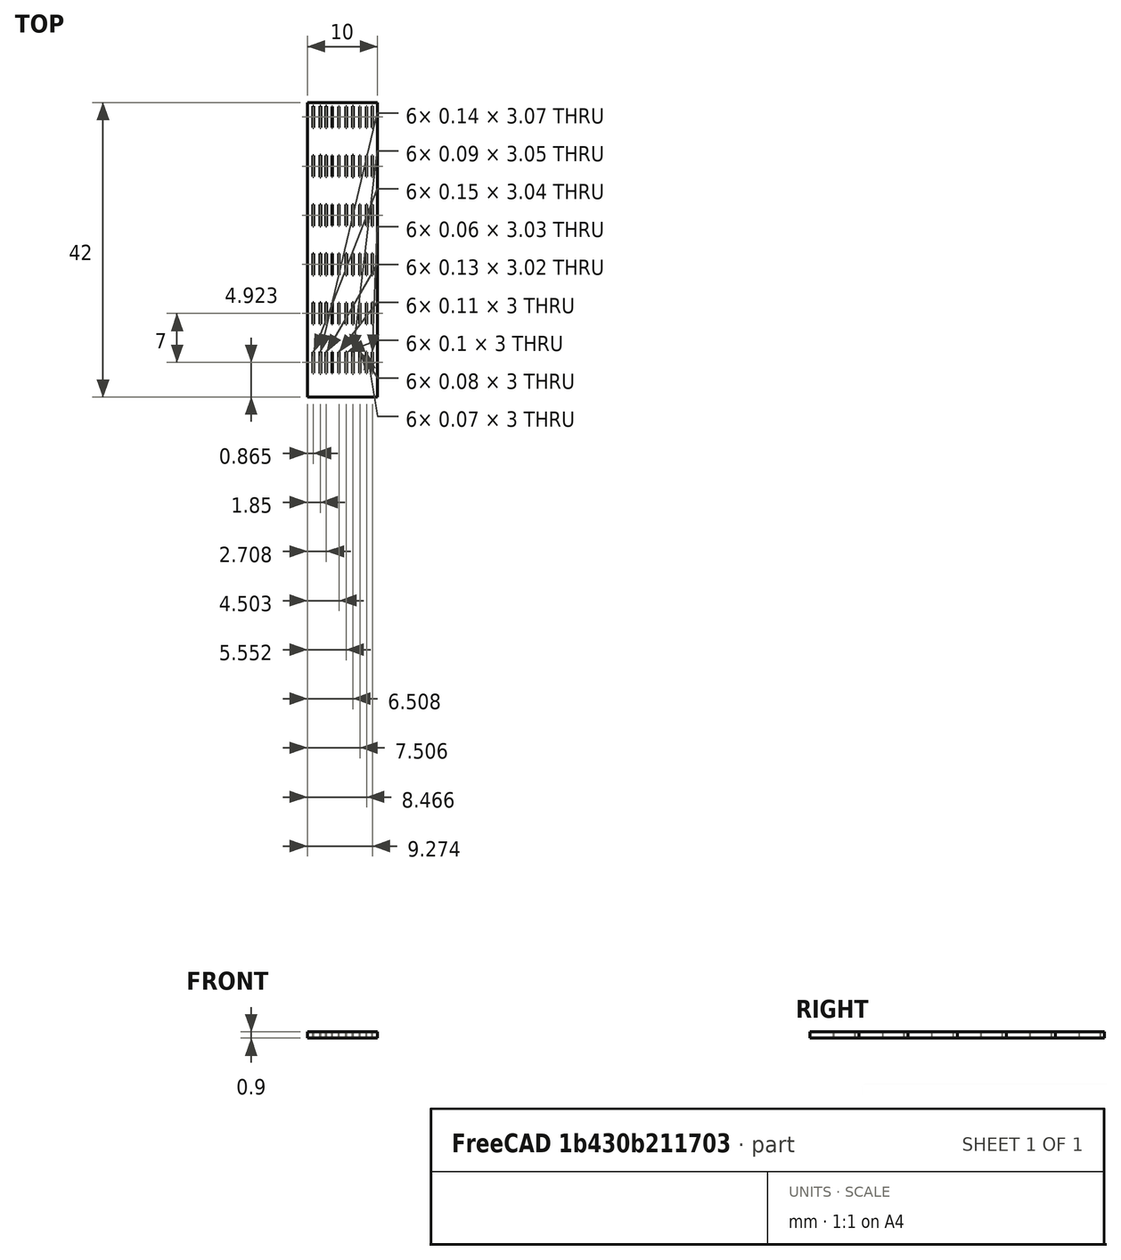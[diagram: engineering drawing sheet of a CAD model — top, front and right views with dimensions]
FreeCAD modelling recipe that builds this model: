
FCSTD DOCUMENT  (FreeCAD 0.20R29177 (Git))
Label: Slit test
License: All rights reserved
LicenseURL: http://en.wikipedia.org/wiki/All_rights_reserved
objects: Sketcher::SketchObject×1, PartDesign::Pad×1, PartDesign::LinearPattern×1, PartDesign::Body×1
note: 5 computed .brp shape members not serialized (recipe doc carries the construction recipe); baked Part::Feature solids carry a one-line shape summary decoded from their .brp

FEATURE [Sketcher::SketchObject] Sketch
  FullyConstrained = false
  MapMode = 5
  Support = -> [XY_Plane]
  sketch-geometry (44):
    g0: LineSegment StartX=0 StartY=0 StartZ=0 EndX=10.0001 EndY=0 EndZ=0
    g1: LineSegment StartX=10.0001 StartY=0 StartZ=0 EndX=10 EndY=7 EndZ=0
    g2: LineSegment StartX=10 StartY=7 StartZ=0 EndX=0 EndY=7 EndZ=0
    g3: LineSegment StartX=0 StartY=7 StartZ=0 EndX=0 EndY=0 EndZ=0
    g4: LineSegment StartX=8.4312 StartY=3.42473 StartZ=0 EndX=8.5012 EndY=3.42473 EndZ=0
    g5: LineSegment StartX=8.5012 StartY=3.42473 StartZ=0 EndX=8.5012 EndY=6.42151 EndZ=0
    g6: LineSegment StartX=8.5012 StartY=6.42151 StartZ=0 EndX=8.4312 EndY=6.42151 EndZ=0
    g7: LineSegment StartX=8.4312 StartY=6.42151 StartZ=0 EndX=8.4312 EndY=3.42473 EndZ=0
    g8: LineSegment StartX=7.54626 StartY=3.42473 StartZ=0 EndX=7.46626 EndY=3.42473 EndZ=0
    g9: LineSegment StartX=7.46626 StartY=3.42473 StartZ=0 EndX=7.46626 EndY=6.42151 EndZ=0
    g10: LineSegment StartX=7.46626 StartY=6.42151 StartZ=0 EndX=7.54626 EndY=6.42151 EndZ=0
    g11: LineSegment StartX=7.54626 StartY=6.42151 StartZ=0 EndX=7.54626 EndY=3.42473 EndZ=0
    g12: LineSegment StartX=5.60229 StartY=3.42473 StartZ=0 EndX=5.50229 EndY=3.42473 EndZ=0
    g13: LineSegment StartX=5.50229 StartY=3.42473 StartZ=0 EndX=5.50229 EndY=6.42151 EndZ=0
    g14: LineSegment StartX=5.50229 StartY=6.42151 StartZ=0 EndX=5.60229 EndY=6.42151 EndZ=0
    g15: LineSegment StartX=5.60229 StartY=6.42151 StartZ=0 EndX=5.60229 EndY=3.42473 EndZ=0
    g16: LineSegment StartX=4.55752 StartY=3.42473 StartZ=0 EndX=4.44752 EndY=3.42473 EndZ=0
    g17: LineSegment StartX=4.44752 StartY=3.42473 StartZ=0 EndX=4.44752 EndY=6.42151 EndZ=0
    g18: LineSegment StartX=4.44752 StartY=6.42151 StartZ=0 EndX=4.55752 EndY=6.42151 EndZ=0
    g19: LineSegment StartX=4.55752 StartY=6.42151 StartZ=0 EndX=4.55752 EndY=3.42473 EndZ=0
    g20: LineSegment StartX=3.60416 StartY=3.42473 StartZ=0 EndX=3.48416 EndY=3.42473 EndZ=0
    g21: LineSegment StartX=3.48416 StartY=3.42473 StartZ=0 EndX=3.48416 EndY=6.42151 EndZ=0
    g22: LineSegment StartX=3.48416 StartY=6.42151 StartZ=0 EndX=3.60416 EndY=6.42151 EndZ=0
    g23: LineSegment StartX=3.60416 StartY=6.42151 StartZ=0 EndX=3.60416 EndY=3.42473 EndZ=0
    g24: LineSegment StartX=9.24385 StartY=6.43941 StartZ=0 EndX=9.30385 EndY=6.43941 EndZ=0
    g25: LineSegment StartX=9.30385 StartY=6.43941 StartZ=0 EndX=9.30385 EndY=3.40683 EndZ=0
    g26: LineSegment StartX=9.30385 StartY=3.40683 StartZ=0 EndX=9.24385 EndY=3.40683 EndZ=0
    g27: LineSegment StartX=9.24385 StartY=3.40683 StartZ=0 EndX=9.24385 EndY=6.43941 EndZ=0
    g28: LineSegment StartX=6.46255 StartY=6.44903 StartZ=0 EndX=6.55255 EndY=6.44903 EndZ=0
    g29: LineSegment StartX=6.55255 StartY=6.44903 StartZ=0 EndX=6.55255 EndY=3.39721 EndZ=0
    g30: LineSegment StartX=6.55255 StartY=3.39721 StartZ=0 EndX=6.46255 EndY=3.39721 EndZ=0
    g31: LineSegment StartX=6.46255 StartY=3.39721 StartZ=0 EndX=6.46255 EndY=6.44903 EndZ=0
    g32: LineSegment StartX=2.77255 StartY=3.41186 StartZ=0 EndX=2.64255 EndY=3.41186 EndZ=0
    g33: LineSegment StartX=2.64255 StartY=3.41186 StartZ=0 EndX=2.64255 EndY=6.43438 EndZ=0
    g34: LineSegment StartX=2.64255 StartY=6.43438 StartZ=0 EndX=2.77255 EndY=6.43438 EndZ=0
    g35: LineSegment StartX=2.77255 StartY=6.43438 StartZ=0 EndX=2.77255 EndY=3.41186 EndZ=0
    g36: LineSegment StartX=1.91982 StartY=3.38684 StartZ=0 EndX=1.77982 EndY=3.38684 EndZ=0
    g37: LineSegment StartX=1.77982 StartY=3.38684 StartZ=0 EndX=1.77982 EndY=6.4594 EndZ=0
    g38: LineSegment StartX=1.77982 StartY=6.4594 StartZ=0 EndX=1.91982 EndY=6.4594 EndZ=0
    g39: LineSegment StartX=1.91982 StartY=6.4594 StartZ=0 EndX=1.91982 EndY=3.38684 EndZ=0
    g40: LineSegment StartX=0.939604 StartY=3.40451 StartZ=0 EndX=0.789604 EndY=3.40451 EndZ=0
    g41: LineSegment StartX=0.789604 StartY=3.40451 StartZ=0 EndX=0.789604 EndY=6.44173 EndZ=0
    g42: LineSegment StartX=0.789604 StartY=6.44173 StartZ=0 EndX=0.939604 EndY=6.44173 EndZ=0
    g43: LineSegment StartX=0.939604 StartY=6.44173 StartZ=0 EndX=0.939604 EndY=3.40451 EndZ=0
  constraints (54):
    c: Coincident(g3,g0)
    c: Horizontal(g0)
    c: Horizontal(g2)
    c: Coincident(g0,g-1)
    c: DistanceY(g1,g1) = 7
    c: Horizontal(g4)
    c: Horizontal(g6)
    c: Vertical(g5)
    c: Horizontal(g8)
    c: Horizontal(g10)
    c: Vertical(g9)
    c: Horizontal(g12)
    c: Horizontal(g14)
    c: Vertical(g13)
    c: Horizontal(g16)
    c: Horizontal(g18)
    c: Vertical(g17)
    c: Horizontal(g20)
    c: Horizontal(g22)
    c: Vertical(g21)
    c: Equal(g7,g11)
    c: Equal(g11,g15)
    c: Equal(g15,g19)
    c: Equal(g19,g23)
    c: DistanceX(g6,g6) = 0.07
    c: DistanceX(g10,g10) = 0.08
    c: Horizontal(g24)
    c: Horizontal(g26)
    c: Vertical(g27)
    c: Horizontal(g28)
    c: Horizontal(g30)
    c: Vertical(g31)
    c: DistanceX(g24,g24) = 0.06
    c: DistanceX(g28,g28) = 0.09
    c: DistanceX(g12,g12) = 0.1
    c: DistanceX(g16,g16) = 0.11
    c: DistanceX(g20,g20) = 0.12
    c: Horizontal(g32)
    c: Horizontal(g34)
    c: Vertical(g33)
    c: Horizontal(g36)
    c: Horizontal(g38)
    c: Vertical(g37)
    c: Horizontal(g40)
    c: Horizontal(g42)
    c: Vertical(g41)
    c: Vertical(g43)
    c: DistanceX(g32,g32) = 0.13
    c: DistanceX(g36,g36) = 0.14
    c: DistanceX(g40,g40) = 0.15
    c: Coincident(g3,g2)
    c: Perpendicular(g2,g3)
    c: Coincident(g0,g1)
    c: Coincident(g1,g2)
FEATURE [PartDesign::Pad] Pad
  Direction = (0,0,1)
  Length = 0.9
  Length2 = 10
  Profile = -> Sketch
  ReferenceAxis = -> Sketch [N_Axis]
  Type = 0
FEATURE [PartDesign::LinearPattern] LinearPattern
  BaseFeature = -> Pad
  Direction = -> Y_Axis
  Length = 35
  Occurrences = 6
  Originals = -> [Pad]
FEATURE [PartDesign::Body] Body
  Group = -> [Sketch,Pad,LinearPattern]
  Origin = -> Origin
  Tip = -> LinearPattern
